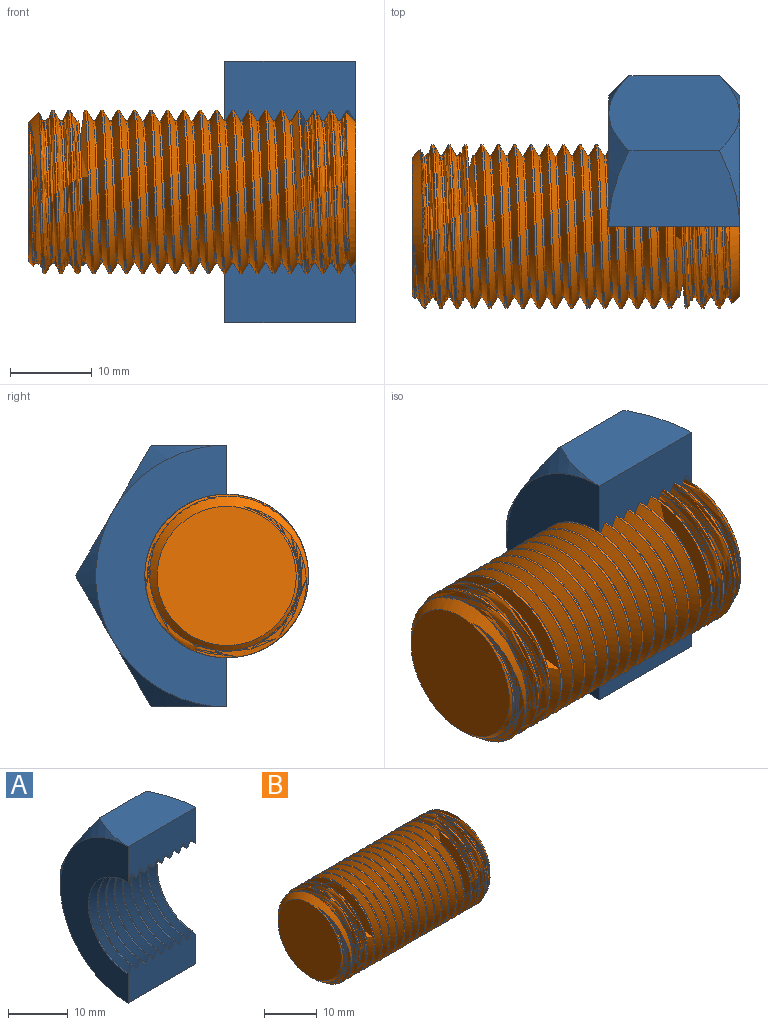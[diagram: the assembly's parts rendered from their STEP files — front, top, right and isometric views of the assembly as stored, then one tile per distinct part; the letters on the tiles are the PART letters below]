
ASSEMBLY  parts=2 mates=1
PART A: 49 faces, bbox 18.6x27.9x37.8 mm
  f0: plane 16x7.3mm, normal (0,-1,0), area 106.4mm2, adj f6,f11,f12,f13,f14,f15,f16,f17
  f1: cone r=18.5mm half-angle=45deg, axis (-1,0,0), area 19.5mm2, adj f2,f4,f47
  f2: plane 16.01x16mm, normal (0,0.87,-0.5), area 264.2mm2, adj f1,f3,f4,f6,f7,f8
  f3: cone r=18.5mm half-angle=45deg, axis (-1,0,0), area 19.5mm2, adj f2,f6,f47
  f4: plane 16.01x16mm, normal (0,0.87,0.5), area 264.2mm2, adj f1,f2,f5,f8,f9,f10
  f5: cone r=18.5mm half-angle=45deg, axis (-1,0,0), area 19.5mm2, adj f4,f9,f47
  f6: plane 16.01x9.24mm, normal (0,0,-1), area 132.1mm2, adj f0,f2,f3,f7
  f7: cone r=18.5mm half-angle=45deg, axis (1,0,0), area 19.5mm2, adj f2,f6,f46
  f8: cone r=18.5mm half-angle=45deg, axis (1,0,0), area 19.5mm2, adj f2,f4,f46
  f9: plane 16.01x9.24mm, normal (0,0,1), area 132.1mm2, adj f4,f5,f10,f48
  f10: cone r=18.5mm half-angle=45deg, axis (1,0,0), area 19.5mm2, adj f4,f9,f46
  f11: bspline ~20.21x20mm, area 44.1mm2, adj f0,f12,f44,f48
  f12: cylinder r=8.7mm len=17.4mm, axis (-1,0,0), area 6.6mm2, adj f0,f11,f13,f47,f48
  f13: bspline ~20x11.55mm, area 21.7mm2, adj f0,f12,f45,f47
  f14: bspline ~20.21x20mm, area 44.1mm2, adj f0,f15,f43,f48
  f15: cylinder r=8.7mm len=17.4mm, axis (-1,0,0), area 6.8mm2, adj f0,f14,f16,f48
  f16: bspline ~20.21x20mm, area 44.1mm2, adj f0,f15,f44,f48
  f17: bspline ~20.21x20mm, area 44.1mm2, adj f0,f18,f42,f48
  f18: cylinder r=8.7mm len=17.4mm, axis (-1,0,0), area 6.8mm2, adj f0,f17,f19,f48
  f19: bspline ~20.21x20mm, area 44.1mm2, adj f0,f18,f43,f48
  f20: bspline ~20.21x20mm, area 44.1mm2, adj f0,f21,f41,f48
  f21: cylinder r=8.7mm len=17.4mm, axis (-1,0,0), area 6.8mm2, adj f0,f20,f22,f48
  f22: bspline ~20.21x20mm, area 44.1mm2, adj f0,f21,f42,f48
  f23: bspline ~20.21x20mm, area 44.1mm2, adj f0,f24,f40,f48
  f24: cylinder r=8.7mm len=17.4mm, axis (-1,0,0), area 6.8mm2, adj f0,f23,f25,f48
  f25: bspline ~20.21x20mm, area 44.1mm2, adj f0,f24,f41,f48
  f26: bspline ~20.21x20mm, area 44.1mm2, adj f0,f27,f39,f48
  f27: cylinder r=8.7mm len=17.4mm, axis (-1,0,0), area 6.8mm2, adj f0,f26,f28,f48
  f28: bspline ~20.21x20mm, area 44.1mm2, adj f0,f27,f40,f48
  f29: bspline ~20.21x20mm, area 44.1mm2, adj f0,f30,f38,f48
  f30: cylinder r=8.7mm len=17.4mm, axis (-1,0,0), area 6.8mm2, adj f0,f29,f31,f48
  f31: bspline ~20.21x20mm, area 44.1mm2, adj f0,f30,f39,f48
  f32: bspline ~20.21x20mm, area 44.1mm2, adj f0,f33,f37,f48
  f33: cylinder r=8.7mm len=17.4mm, axis (-1,0,0), area 6.8mm2, adj f0,f32,f34,f48
  f34: bspline ~20.21x20mm, area 44.1mm2, adj f0,f33,f38,f48
  f35: cylinder r=8.7mm len=3.37mm, axis (-1,0,0), area 0.2mm2, adj f36,f46,f48
  f36: bspline ~20.21x20mm, area 22.4mm2, adj f35,f37,f46,f48
  f37: cylinder r=10mm len=20mm, axis (-1,0,0), area 7.6mm2, adj f0,f32,f36,f46,f48
  f38: cylinder r=10mm len=20mm, axis (-1,0,0), area 7.9mm2, adj f0,f29,f34,f48
  f39: cylinder r=10mm len=20mm, axis (-1,0,0), area 7.9mm2, adj f0,f26,f31,f48
  f40: cylinder r=10mm len=20mm, axis (-1,0,0), area 7.9mm2, adj f0,f23,f28,f48
  f41: cylinder r=10mm len=20mm, axis (-1,0,0), area 7.9mm2, adj f0,f20,f25,f48
  f42: cylinder r=10mm len=20mm, axis (-1,0,0), area 7.9mm2, adj f0,f17,f22,f48
  f43: cylinder r=10mm len=20mm, axis (-1,0,0), area 7.9mm2, adj f0,f14,f19,f48
  f44: cylinder r=10mm len=20mm, axis (-1,0,0), area 7.9mm2, adj f0,f11,f16,f48
  f45: cylinder r=10mm len=3.88mm, axis (-1,0,0), area 0.2mm2, adj f0,f13,f47
  f46: plane 32.81x16.81mm, normal (-1,0,0), area 264.5mm2, adj f0,f7,f8,f10,f35,f36,f37,f48
  f47: plane 32.81x16.81mm, normal (1,0,0), area 264.5mm2, adj f0,f1,f3,f5,f12,f13,f45,f48
  f48: plane 16x7.3mm, normal (0,-1,0), area 106.4mm2, adj f9,f11,f12,f14,f15,f16,f17,f18
PART B: 8 faces, bbox 41.8x23.1x20 mm
  f0: plane 17x17mm, normal (1,0,0), area 227mm2, adj f3
  f1: cylinder r=10mm len=37mm, axis (-1,0,0), area 568.4mm2, adj f3,f4,f5,f7
  f2: plane 17x17mm, normal (-1,0,0), area 227mm2, adj f4
  f3: cone r=10mm half-angle=45deg, axis (-1,0,0), area 68.4mm2, adj f0,f1,f5,f6,f7
  f4: cone r=8.5mm half-angle=45deg, axis (1,0,0), area 68.4mm2, adj f1,f2,f5,f6,f7
  f5: bspline ~40.75x23.09mm, area 1706.6mm2, adj f1,f3,f4,f6
  f6: cylinder r=8.7mm len=39.6mm, axis (-1,0,0), area 259.2mm2, adj f3,f4,f5,f7
  f7: bspline ~40.75x23.09mm, area 1686.1mm2, adj f1,f3,f4,f6
PLACE A t=(2.56,-3.23,6.79)mm
PLACE B t=(-9.44,-3.23,6.79)mm fixed
MATE cylindrical A.f1 <-> B.f1  axis (1,0,0) through (10.56,-3.23,6.79)mm
